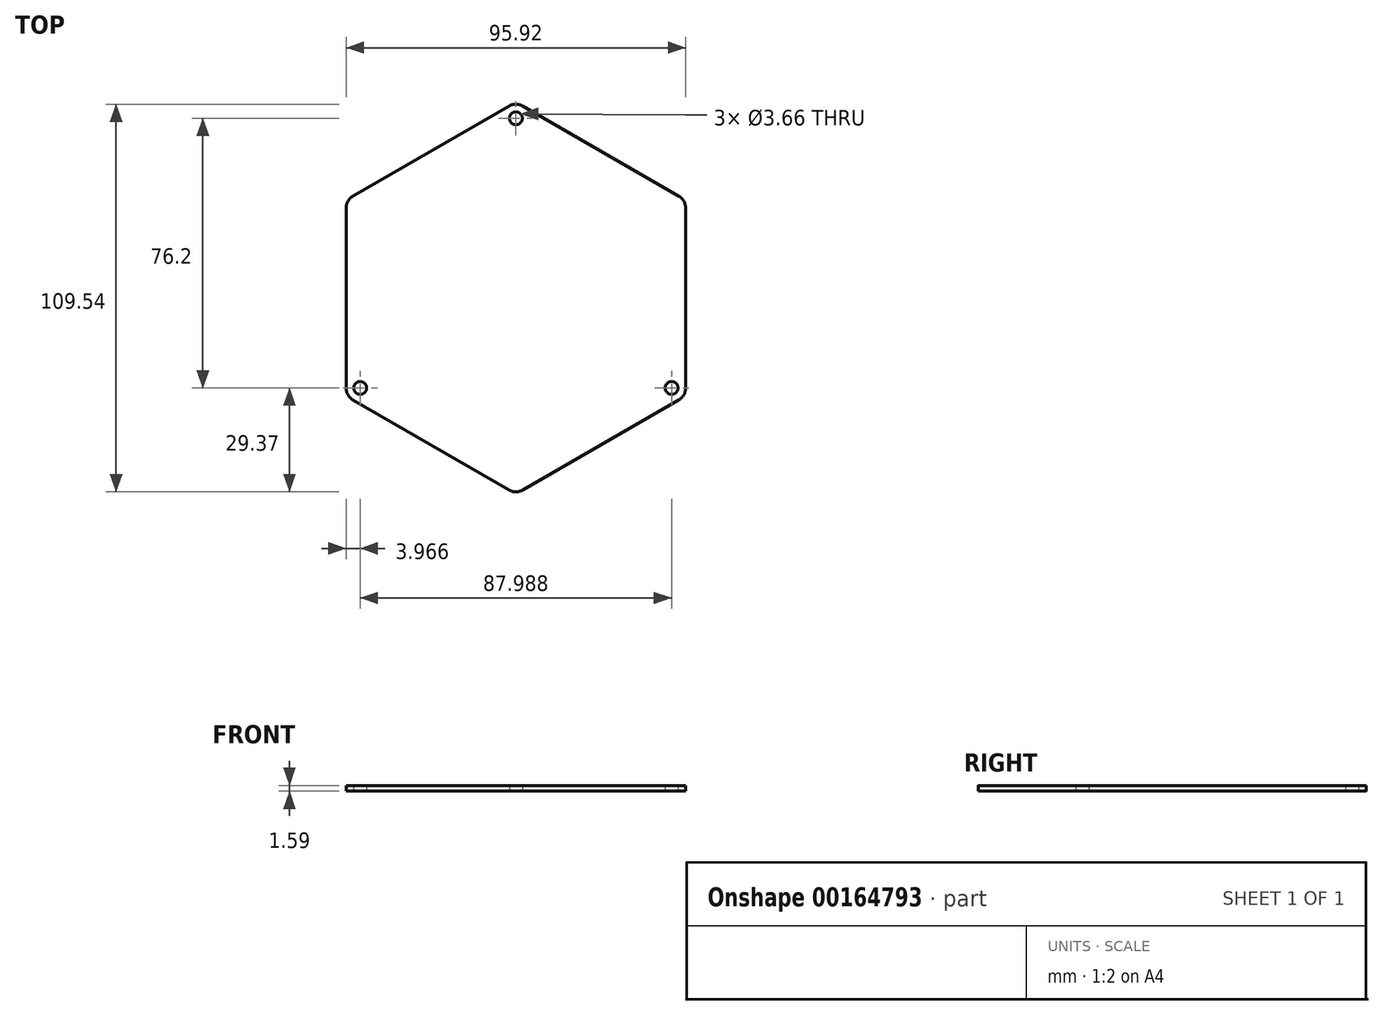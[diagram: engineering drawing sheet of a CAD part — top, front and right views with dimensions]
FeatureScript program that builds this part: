
annotation { "Feature Type Name" : "Feature", "Feature Type Description" : "" }
export const myFeature = defineFeature(function(context is Context, id is Id, definition is map)
    precondition{}
    {
        {
            var Q0;
            Q0=qCreatedBy(makeId("Top.planeOp"),FACE);
            var sketch = newSketch(context, id + "F0", { "sketchPlane" : qUnion([Q0])});
            skPoint(sketch, "E0.middle", {"position": v(0, 0) * mm});
            skLineSegment(sketch, "E1", {"start": v(0, 0) * mm, "end": v(0, 50.8) * mm, "construction": true});
            skLineSegment(sketch, "E2", {"start": v(0, 50.8) * mm, "end": v(44, -25.4) * mm, "construction": true});
            skLineSegment(sketch, "E3", {"start": v(44, -25.4) * mm, "end": v(0, 0) * mm, "construction": true});
            skLineSegment(sketch, "E4", {"start": v(0, 50.8) * mm, "end": v(-44, -25.4) * mm, "construction": true});
            skLineSegment(sketch, "E5", {"start": v(-44, -25.4) * mm, "end": v(0, 0) * mm, "construction": true});
            skLineSegment(sketch, "E6", {"start": v(-44, -25.4) * mm, "end": v(44, -25.4) * mm, "construction": true});
            skCircle(sketch, "E7", {"center": v(0, 50.8) * mm, "radius": 1.83 * mm});
            skCircle(sketch, "E8", {"center": v(44, -25.4) * mm, "radius": 1.83 * mm});
            skCircle(sketch, "E9", {"center": v(-44, -25.4) * mm, "radius": 1.83 * mm});
            skCircle(sketch, "E10", {"center": v(0, 50.8) * mm, "radius": 3.97 * mm, "construction": true});
            skCircle(sketch, "E11.cCircle", {"center": v(0, 0) * mm, "radius": 47.96 * mm, "construction": true});
            skLineSegment(sketch, "E11.0", {"start": v(0, 55.38) * mm, "end": v(47.96, 27.7) * mm});
            skLineSegment(sketch, "E11.1", {"start": v(47.96, 27.7) * mm, "end": v(47.96, -27.7) * mm});
            skLineSegment(sketch, "E11.2", {"start": v(47.96, -27.7) * mm, "end": v(0, -55.38) * mm});
            skLineSegment(sketch, "E11.3", {"start": v(0, -55.38) * mm, "end": v(-47.96, -27.7) * mm});
            skLineSegment(sketch, "E11.4", {"start": v(-47.96, -27.7) * mm, "end": v(-47.96, 27.7) * mm});
            skLineSegment(sketch, "E11.5", {"start": v(-47.96, 27.7) * mm, "end": v(0, 55.38) * mm});
            skPoint(sketch, "E11.0.midPoint", {"position": v(23.98, 41.54) * mm});
            skSolve(sketch);
        }
        {
            var Q0;
            Q0 = qSketchRegion(id + "F0", true);
            extrude(context, id + "F1", {"entities" : qUnion([Q0]), "depth" : 1.59 * mm});
        }
        {
            var Q0;
            Q0=makeQuery(id+"F1.opExtrude","SWEPT_EDGE",EDGE,{"disambiguationData":[OSD([sQuery(id+"F0.wireOp",EDGE,"E11.3"),sQuery(id+"F0.wireOp",EDGE,"E11.4")])]});
            var Q1;
            Q1=makeQuery(id+"F1.opExtrude","SWEPT_EDGE",EDGE,{"disambiguationData":[OSD([sQuery(id+"F0.wireOp",EDGE,"E11.2"),sQuery(id+"F0.wireOp",EDGE,"E11.3")])]});
            var Q2;
            Q2=makeQuery(id+"F1.opExtrude","SWEPT_EDGE",EDGE,{"disambiguationData":[OSD([sQuery(id+"F0.wireOp",EDGE,"E11.1"),sQuery(id+"F0.wireOp",EDGE,"E11.2")])]});
            var Q3;
            Q3=makeQuery(id+"F1.opExtrude","SWEPT_EDGE",EDGE,{"disambiguationData":[OSD([sQuery(id+"F0.wireOp",EDGE,"E11.0"),sQuery(id+"F0.wireOp",EDGE,"E11.1")])]});
            var Q4;
            Q4=makeQuery(id+"F1.opExtrude","SWEPT_EDGE",EDGE,{"disambiguationData":[OSD([sQuery(id+"F0.wireOp",EDGE,"E11.0"),sQuery(id+"F0.wireOp",EDGE,"E11.5")])]});
            var Q5;
            Q5=makeQuery(id+"F1.opExtrude","SWEPT_EDGE",EDGE,{"disambiguationData":[OSD([sQuery(id+"F0.wireOp",EDGE,"E11.4"),sQuery(id+"F0.wireOp",EDGE,"E11.5")])]});
            fillet(context, id + "F2", {"entities" : qUnion([Q0, Q1, Q2, Q3, Q4, Q5]), "radius" : 3.97 * mm, "tangentPropagation" : true, "allowEdgeOverflow" : false});
        }
    });
